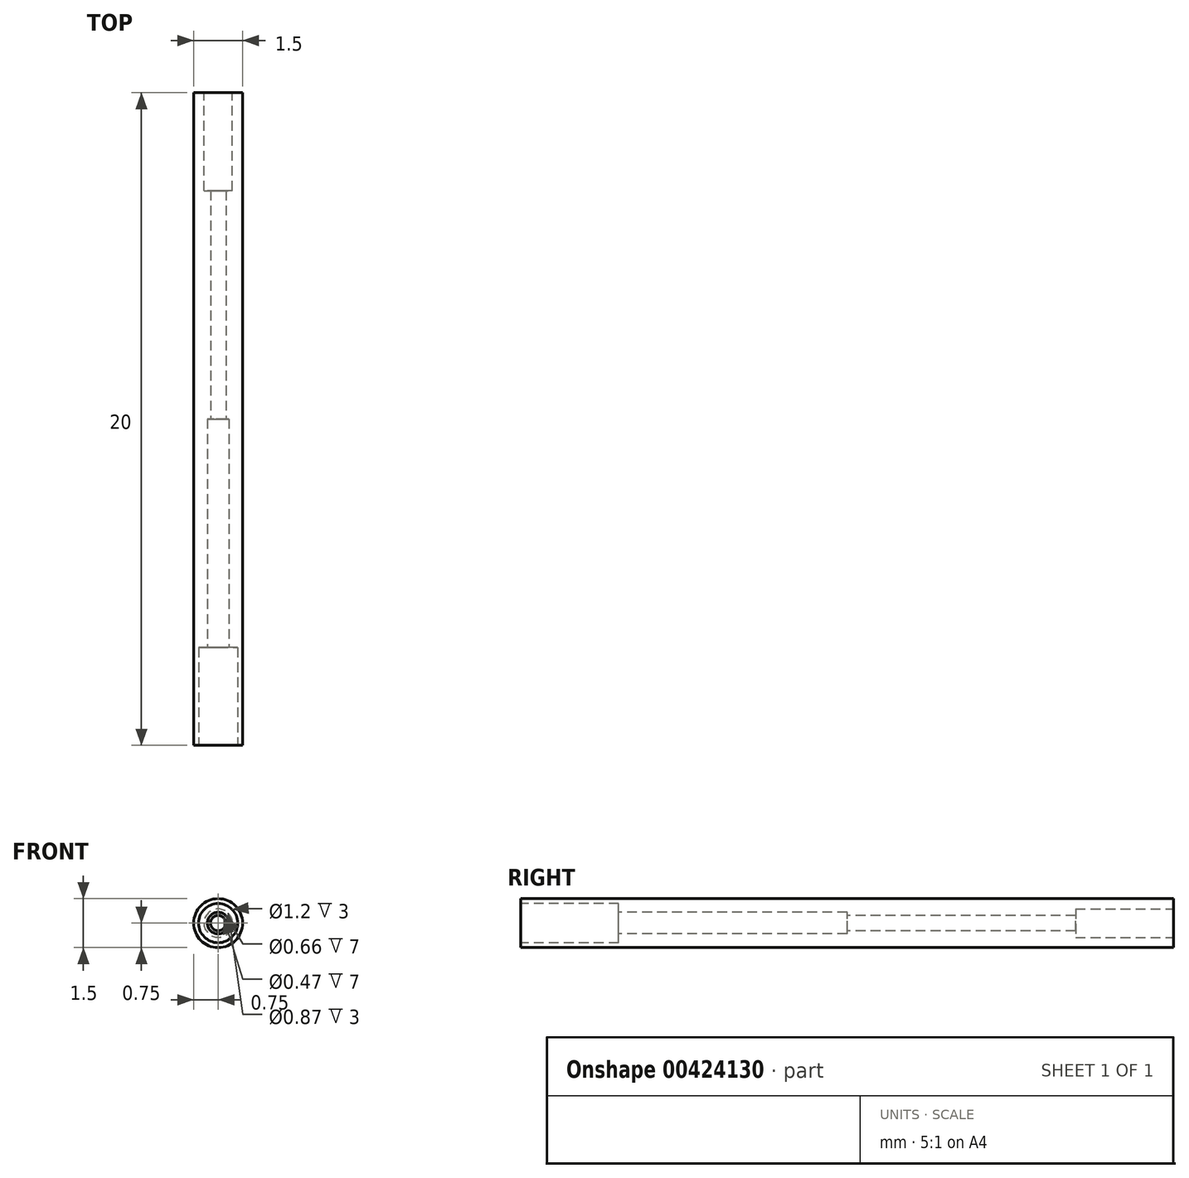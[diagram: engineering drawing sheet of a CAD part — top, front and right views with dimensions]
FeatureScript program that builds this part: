
annotation { "Feature Type Name" : "Feature", "Feature Type Description" : "" }
export const myFeature = defineFeature(function(context is Context, id is Id, definition is map)
    precondition{}
    {
        {
            var Q0;
            Q0=qCreatedBy(makeId("Front.planeOp"),FACE);
            var sketch = newSketch(context, id + "F0", { "sketchPlane" : qUnion([Q0])});
            skCircle(sketch, "E0", {"center": v(0, 0) * mm, "radius": 0.75 * mm});
            skSolve(sketch);
        }
        {
            var Q0;
            Q0 = qSketchRegion(id + "F0", true);
            extrude(context, id + "F1", {"entities" : qUnion([Q0]), "depth" : 20 * mm});
        }
        {
            var Q0;
            Q0=makeQuery(id+"F1.opExtrude","CAP_FACE",FACE,{"disambiguationData":[OSD([sQuery(id+"F0.wireOp",EDGE,"E0")])],"isStart":false});
            var sketch = newSketch(context, id + "F2", { "sketchPlane" : qUnion([Q0])});
            skCircle(sketch, "E1", {"center": v(0, 0) * mm, "radius": 0.6 * mm});
            skSolve(sketch);
        }
        {
            var Q0;
            Q0 = qSketchRegion(id + "F2", true);
            extrude(context, id + "F3", {"entities" : qUnion([Q0]), "operationType" : NewBodyOperationType.REMOVE, "oppositeDirection" : true, "depth" : 3 * mm});
        }
        {
            var Q0;
            Q0=makeQuery(id+"F3.boolean.opBoolean","COPY",FACE,{"derivedFrom":makeQuery(id+"F3.opExtrude","CAP_FACE",FACE,{"disambiguationData":[OSD([sQuery(id+"F2.wireOp",EDGE,"E1")])],"isStart":false})});
            var sketch = newSketch(context, id + "F4", { "sketchPlane" : qUnion([Q0])});
            skCircle(sketch, "E2", {"center": v(0, 0) * mm, "radius": 0.33 * mm});
            skSolve(sketch);
        }
        {
            var Q0;
            Q0 = qSketchRegion(id + "F4", true);
            extrude(context, id + "F5", {"entities" : qUnion([Q0]), "operationType" : NewBodyOperationType.REMOVE, "oppositeDirection" : true, "depth" : 7 * mm});
        }
        {
            var Q0;
            Q0=makeQuery(id+"F5.boolean.opBoolean","COPY",FACE,{"derivedFrom":makeQuery(id+"F5.opExtrude","CAP_FACE",FACE,{"disambiguationData":[OSD([sQuery(id+"F4.wireOp",EDGE,"E2")])],"isStart":false})});
            var sketch = newSketch(context, id + "F6", { "sketchPlane" : qUnion([Q0])});
            skCircle(sketch, "E3", {"center": v(0, 0) * mm, "radius": 0.23 * mm});
            skSolve(sketch);
        }
        {
            var Q0;
            Q0 = qSketchRegion(id + "F6", true);
            var Q1;
            Q1 = qSketchRegion(id + "F4", true);
            extrude(context, id + "F7", {"entities" : qUnion([Q0, Q1]), "operationType" : NewBodyOperationType.REMOVE, "oppositeDirection" : true, "depth" : 7 * mm});
        }
        {
            var Q0;
            Q0=makeQuery(id+"F1.opExtrude","CAP_FACE",FACE,{"disambiguationData":[OSD([sQuery(id+"F0.wireOp",EDGE,"E0")])],"isStart":true});
            var sketch = newSketch(context, id + "F8", { "sketchPlane" : qUnion([Q0])});
            skCircle(sketch, "E4", {"center": v(0, 0) * mm, "radius": 0.43 * mm});
            skSolve(sketch);
        }
        {
            var Q0;
            Q0 = qSketchRegion(id + "F8", true);
            extrude(context, id + "F9", {"entities" : qUnion([Q0]), "operationType" : NewBodyOperationType.REMOVE, "oppositeDirection" : true, "depth" : 3 * mm});
        }
    });
